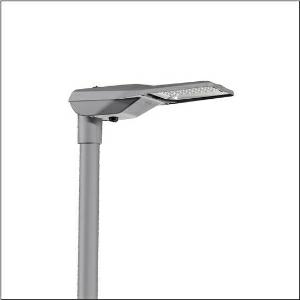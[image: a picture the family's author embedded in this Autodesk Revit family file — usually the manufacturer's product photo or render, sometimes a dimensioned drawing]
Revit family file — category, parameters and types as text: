
# Revit family: streetlight_sl_21_mini___st1_0ab_5xe2m33t08hb_c013
name_source: partatom
category: Lighting Fixtures
units: mm (PartAtom-declared; Revit-internal decimal feet)

## family parameters
Cut with Voids When Loaded = No
Host = Face
Light Source = No
Part Type = Normal
Room Calculation Point = No
Round Connector Dimension = Use Diameter
Shared = No

## types (1)
- --- (1 x LED, 7960 lm, 66 W, 3000K)
    Apparent Load = 66 VA
    CIE Flux Codes = 38 73 97 100 100
    Color Rendering = 70
    Color Temperature = 3000K
    Default Elevation = 1800 mm
    Description = Streetlight SL 21 mini, mast luminaire, primary light control with lens, of PMMA, primary optical cover: cover, of toughened safety glass, transparent, light distribution: ST1.0aB, light emission: direct distribution, primary light characteristic: asymmetric, installation type: side-entry, post-top, LED, High Power LED, rated luminous flux: 7.960lm, luminous efficacy: 121lm/W, light colour: 730, colour temperature: 3000K, control gear: D4i, control: flexible luminous flux parameterisation, time-dependent luminous flux control, constant luminous flux control, overheat protection, pre-setting: logarithmic dimming characteristic, mains connection: 220..240V, AC, 50/60Hz, start of lifetime: 66W, end of service life: 69W, reduction: 30W, luminaire housing, of diecast aluminium, powder-coated, Siteco® metallic grey (DB 702S), corrosivity category C5 mid according to DIN EN ISO 12944, please order mast flange separately, inclination adjustable: 0°, 5°, 10°, 15°, sealing non-destructively replaceable, multi-level sealing system, length: 628mm, width: 235mm, height: 110mm, mast flange for spigot size: 42mm (side-entry): 5XC10008XM4, 60/48mm (side-entry/post-top): 5XC10108XM2, 76/60mm (side-entry/post-top): 5XC10108XM1, mounting height: 4..8m, Smart Interface below and above, protection rating (complete): IP66, insulation class (complete): insulation class II (safety insulation), certification: CE, ENEC, ENEC+, VDE, impact resistance: IK10, permissible operating ambient temperature for outdoor applications: -40..+50°C, standard-compliant lighting for roads and squares, packaging unit: 1 piece

Light Distribution: ST1.0aB
    Height = 110 mm
    Lamp = 1 x LED
    Lamp Light Flux = 7960 lm
    Lamp Power = 66 W
    Lamp count = 1
    Length = 625 mm
    Luminous efficacy = 121 lm/W
    Manufacturer = Siteco
    ModVariant = No
    Model = 5XE2M33T08HB
    Number of Poles = 1
    OnlyDefault = Yes
    Power Factor = 1
    Product Name = Streetlight SL 21 mini | ST1.0aB
    Product group = mast luminaire | pylon top
    ProductGroupID = 6100
    Protection Class = Protection class II
    Protection Degree = IP 66
    RLX_Detail_Level = 1
    RLX_Emergency_Light_Flux = 0 lm
    RLX_Emergency_Type = 0
    RLX_Emergency_Type_DB = No
    RlxData = <blob elided: 26197 chars, md5=b4471e07>
    Socket = socket
    Standby Power = 0 W
    System Light Flux = 7960 lm
    System Power = 66 W
    Type Comments = factory setting: luminous flux: 100 % | dim-lin: 254 | 670 mA
    Type Image = l_1003514.jpg
    URL = http://relux.com
    VarID = @adj_182506
    Voltage = 0 V
    Weight = 0.00 kg
    Width = 234 mm

## geometry (parser evidence)
native form markers: Blend x4, Sweep x11
no freeform markers — native parametric forms only
